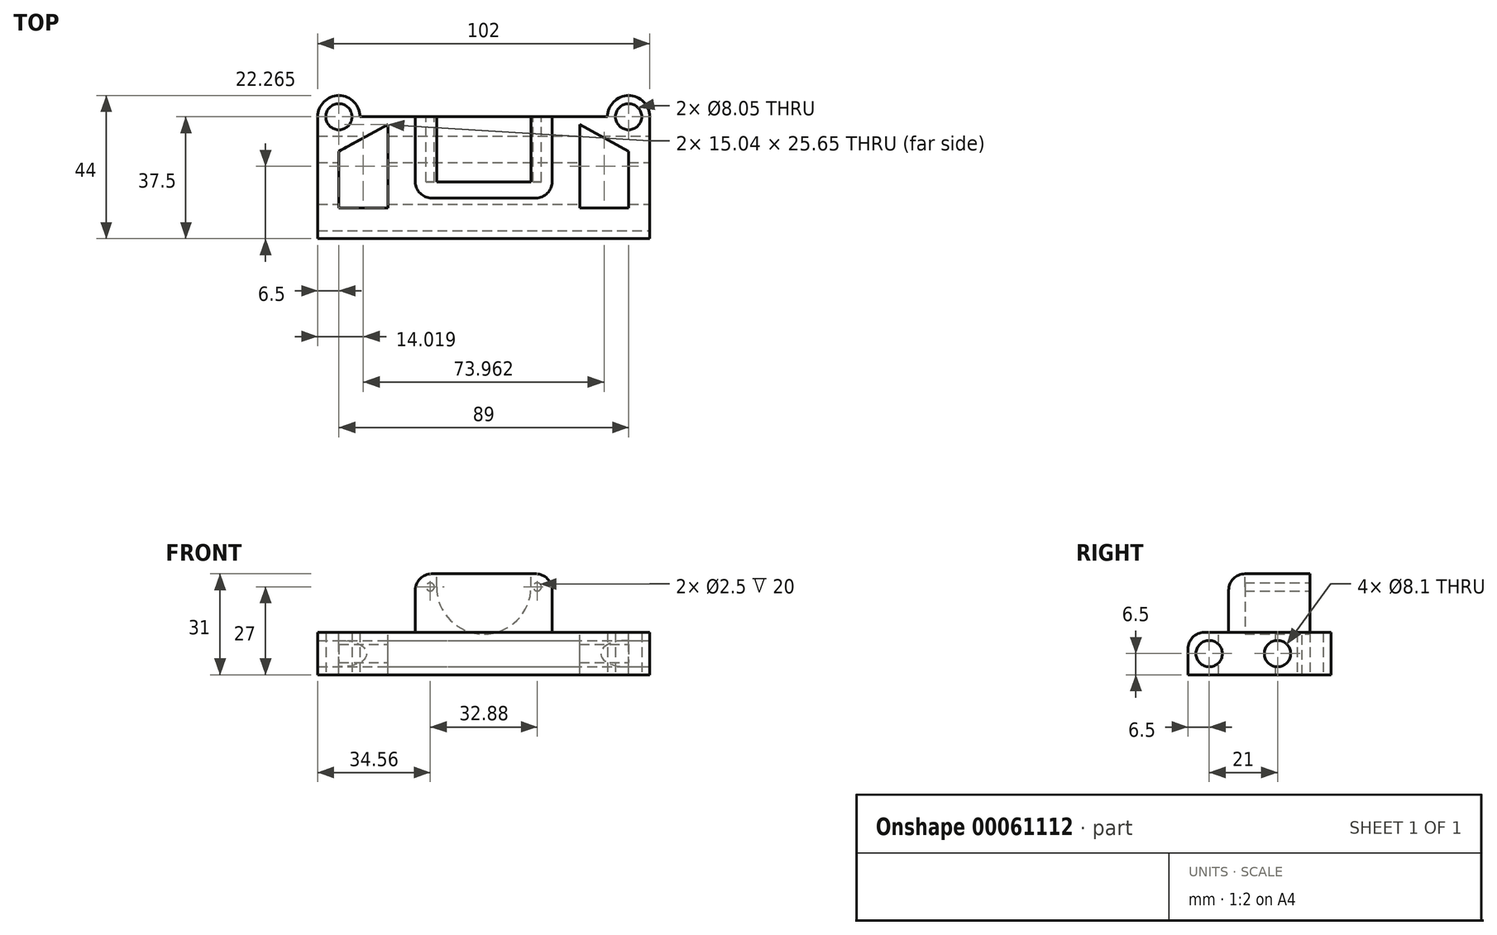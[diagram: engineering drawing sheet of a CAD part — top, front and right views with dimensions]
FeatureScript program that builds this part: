
annotation { "Feature Type Name" : "Feature", "Feature Type Description" : "" }
export const myFeature = defineFeature(function(context is Context, id is Id, definition is map)
    precondition{}
    {
        {
            var Q0;
            Q0=qCreatedBy(makeId("Top.planeOp"),FACE);
            var sketch = newSketch(context, id + "F0", { "sketchPlane" : qUnion([Q0])});
            skLineSegment(sketch, "E0", {"start": v(0, 0) * mm, "end": v(-38, 0) * mm});
            skLineSegment(sketch, "E1", {"start": v(0, 0) * mm, "end": v(38, 0) * mm});
            skCircle(sketch, "E2", {"center": v(-44.5, 0) * mm, "radius": 4.03 * mm});
            skCircle(sketch, "E3", {"center": v(44.5, 0) * mm, "radius": 4.03 * mm});
            skArc(sketch, "E4", {"start": v(-38, 0) * mm, "mid": v(-44.5, 6.5) * mm, "end": v(-51, 0) * mm});
            skArc(sketch, "E5", {"start": v(51, 0) * mm, "mid": v(44.5, 6.5) * mm, "end": v(38, 0) * mm});
            skLineSegment(sketch, "E6", {"start": v(0, 0) * mm, "end": v(0, -37.5) * mm, "construction": true});
            skLineSegment(sketch, "E7", {"start": v(0, -37.5) * mm, "end": v(-51, -37.5) * mm});
            skLineSegment(sketch, "E8", {"start": v(0, -37.5) * mm, "end": v(51, -37.5) * mm});
            skLineSegment(sketch, "E9", {"start": v(-51, -37.5) * mm, "end": v(-51, 0) * mm});
            skLineSegment(sketch, "E10", {"start": v(51, -37.5) * mm, "end": v(51, 0) * mm});
            skSolve(sketch);
        }
        {
            var Q0;
            Q0 = qSketchRegion(id + "F0", true);
            var Q1;
            Q1=makeQuery(id+"F0.imprint","IMPRINT",FACE,{"disambiguationData":[TD([[makeQuery(id+"F0.imprint","IMPRINT",EDGE,{"derivedFrom":sQuery(id+"F0.wireOp",EDGE,"E0")}),1.0]])]});
            extrude(context, id + "F1", {"entities" : qUnion([Q0, Q1]), "depth" : 13 * mm});
        }
        {
            var Q0;
            Q0=makeQuery(id+"F1.opExtrude","SWEPT_FACE",FACE,{"disambiguationData":[OSD([sQuery(id+"F0.wireOp",EDGE,"E10")])]});
            var sketch = newSketch(context, id + "F2", { "sketchPlane" : qUnion([Q0])});
            skCircle(sketch, "E11", {"center": v(-10, 6.5) * mm, "radius": 4.05 * mm});
            skCircle(sketch, "E12", {"center": v(-31, 6.5) * mm, "radius": 4.05 * mm});
            skLineSegment(sketch, "E13", {"start": v(0, 6.5) * mm, "end": v(-10, 6.5) * mm, "construction": true});
            skLineSegment(sketch, "E14", {"start": v(-10, 6.5) * mm, "end": v(-31, 6.5) * mm, "construction": true});
            skSolve(sketch);
        }
        {
            var Q0;
            Q0=makeQuery(id+"F2.imprint","IMPRINT",FACE,{"disambiguationData":[TD([[makeQuery(id+"F2.imprint","IMPRINT",EDGE,{"derivedFrom":sQuery(id+"F2.wireOp",EDGE,"E12")}),1.0]])]});
            var Q1;
            Q1=makeQuery(id+"F2.imprint","IMPRINT",FACE,{"disambiguationData":[TD([[makeQuery(id+"F2.imprint","IMPRINT",EDGE,{"derivedFrom":sQuery(id+"F2.wireOp",EDGE,"E11")}),1.0]])]});
            extrude(context, id + "F3", {"entities" : qUnion([Q0, Q1]), "operationType" : NewBodyOperationType.REMOVE, "oppositeDirection" : true, "depth" : 120 * mm});
        }
        {
            var Q0;
            Q0=makeQuery(id+"F1.opExtrude","CAP_FACE",FACE,{"disambiguationData":[OSD([sQuery(id+"F0.wireOp",EDGE,"E0"),sQuery(id+"F0.wireOp",EDGE,"E1"),sQuery(id+"F0.wireOp",EDGE,"E2"),sQuery(id+"F0.wireOp",EDGE,"E3"),sQuery(id+"F0.wireOp",EDGE,"E4"),sQuery(id+"F0.wireOp",EDGE,"E5"),sQuery(id+"F0.wireOp",EDGE,"E7"),sQuery(id+"F0.wireOp",EDGE,"E8"),sQuery(id+"F0.wireOp",EDGE,"E9"),sQuery(id+"F0.wireOp",EDGE,"E10")])],"isStart":false});
            var sketch = newSketch(context, id + "F4", { "sketchPlane" : qUnion([Q0])});
            skLineSegment(sketch, "E15", {"start": v(0, 0) * mm, "end": v(0, -25) * mm, "construction": true});
            skLineSegment(sketch, "E16", {"start": v(0, -25) * mm, "end": v(-21, -25) * mm});
            skLineSegment(sketch, "E17", {"start": v(-21, -25) * mm, "end": v(-21, 0) * mm});
            skLineSegment(sketch, "E18", {"start": v(0, -25) * mm, "end": v(21, -25) * mm});
            skLineSegment(sketch, "E19", {"start": v(21, -25) * mm, "end": v(21, 0) * mm});
            skLineSegment(sketch, "E20", {"start": v(21, 0) * mm, "end": v(-21, 0) * mm});
            skSolve(sketch);
        }
        {
            var Q0;
            Q0=makeQuery(id+"F4.imprint","IMPRINT",FACE,{"disambiguationData":[TD([[makeQuery(id+"F4.imprint","IMPRINT",EDGE,{"derivedFrom":sQuery(id+"F4.wireOp",EDGE,"E16")}),-1.0]])]});
            extrude(context, id + "F5", {"entities" : qUnion([Q0]), "operationType" : NewBodyOperationType.ADD, "depth" : 18 * mm});
        }
        {
            var Q0;
            Q0=makeQuery(id+"F5.boolean.opBoolean","MERGE",FACE,{"derivedFrom":[makeQuery(id+"F1.opExtrude","SWEPT_FACE",FACE,{"disambiguationData":[OSD([sQuery(id+"F0.wireOp",EDGE,"E0"),sQuery(id+"F0.wireOp",EDGE,"E1")])]}),makeQuery(id+"F5.opExtrude","SWEPT_FACE",FACE,{"disambiguationData":[OSD([sQuery(id+"F4.wireOp",EDGE,"E20")])]})]});
            var sketch = newSketch(context, id + "F6", { "sketchPlane" : qUnion([Q0])});
            skLineSegment(sketch, "E21", {"start": v(0, 31) * mm, "end": v(0, 27) * mm, "construction": true});
            skPoint(sketch, "E21.endSnap0", {"position": v(0, 31) * mm});
            skArc(sketch, "E22", {"start": v(-14.5, 27) * mm, "mid": v(0, 12.5) * mm, "end": v(14.5, 27) * mm});
            skLineSegment(sketch, "E23", {"start": v(0, 27) * mm, "end": v(-16.44, 27) * mm, "construction": true});
            skLineSegment(sketch, "E24", {"start": v(0, 27) * mm, "end": v(16.44, 27) * mm, "construction": true});
            skCircle(sketch, "E25", {"center": v(-16.44, 27) * mm, "radius": 1.25 * mm});
            skCircle(sketch, "E26", {"center": v(16.44, 27) * mm, "radius": 1.25 * mm});
            skLineSegment(sketch, "E27", {"start": v(-14.5, 27) * mm, "end": v(-14.5, 31) * mm});
            skLineSegment(sketch, "E28", {"start": v(14.5, 27) * mm, "end": v(14.5, 31) * mm});
            skSolve(sketch);
        }
        {
            var Q0;
            Q0=makeQuery(id+"F6.imprint","IMPRINT",FACE,{"disambiguationData":[TD([[makeQuery(id+"F6.imprint","IMPRINT",EDGE,{"derivedFrom":sQuery(id+"F6.wireOp",EDGE,"E22")}),1.0]])]});
            var Q1;
            Q1=makeQuery(id+"F6.imprint","IMPRINT",FACE,{"disambiguationData":[TD([[makeQuery(id+"F6.imprint","IMPRINT",EDGE,{"derivedFrom":sQuery(id+"F6.wireOp",EDGE,"E25")}),1.0]])]});
            var Q2;
            Q2=makeQuery(id+"F6.imprint","IMPRINT",FACE,{"disambiguationData":[TD([[makeQuery(id+"F6.imprint","IMPRINT",EDGE,{"derivedFrom":sQuery(id+"F6.wireOp",EDGE,"E26")}),1.0]])]});
            extrude(context, id + "F7", {"entities" : qUnion([Q0, Q1, Q2]), "operationType" : NewBodyOperationType.REMOVE, "oppositeDirection" : true, "depth" : 20 * mm});
        }
        {
            var Q0;
            Q0=makeQuery(id+"F5.opExtrude","CAP_EDGE",EDGE,{"disambiguationData":[OSD([sQuery(id+"F4.wireOp",EDGE,"E19")])],"isStart":false});
            var Q1;
            Q1=makeQuery(id+"F5.opExtrude","CAP_EDGE",EDGE,{"disambiguationData":[OSD([sQuery(id+"F4.wireOp",EDGE,"E17")])],"isStart":false});
            var Q2;
            Q2=makeQuery(id+"F5.opExtrude","CAP_EDGE",EDGE,{"disambiguationData":[OSD([sQuery(id+"F4.wireOp",EDGE,"E19")])],"isStart":true});
            var Q3;
            Q3=makeQuery(id+"F5.opExtrude","CAP_EDGE",EDGE,{"disambiguationData":[OSD([sQuery(id+"F4.wireOp",EDGE,"E17")])],"isStart":true});
            var Q4;
            Q4=makeQuery(id+"F5.opExtrude","CAP_EDGE",EDGE,{"disambiguationData":[OSD([sQuery(id+"F4.wireOp",EDGE,"E16"),sQuery(id+"F4.wireOp",EDGE,"E18")])],"isStart":false});
            var Q5;
            Q5=makeQuery(id+"F5.opExtrude","SWEPT_EDGE",EDGE,{"disambiguationData":[OSD([sQuery(id+"F4.wireOp",EDGE,"E18"),sQuery(id+"F4.wireOp",EDGE,"E19")])]});
            var Q6;
            Q6=makeQuery(id+"F5.opExtrude","SWEPT_EDGE",EDGE,{"disambiguationData":[OSD([sQuery(id+"F4.wireOp",EDGE,"E16"),sQuery(id+"F4.wireOp",EDGE,"E17")])]});
            var Q7;
            Q7=makeQuery(id+"F1.opExtrude","CAP_EDGE",EDGE,{"disambiguationData":[OSD([sQuery(id+"F0.wireOp",EDGE,"E7"),sQuery(id+"F0.wireOp",EDGE,"E8")])],"isStart":false});
            fillet(context, id + "F8", {"entities" : qUnion([Q0, Q1, Q2, Q3, Q4, Q5, Q6, Q7]), "radius" : 5 * mm, "tangentPropagation" : true, "allowEdgeOverflow" : false});
        }
        {
            var Q0;
            Q0=makeQuery(id+"F1.opExtrude","CAP_FACE",FACE,{"disambiguationData":[OSD([sQuery(id+"F0.wireOp",EDGE,"E0"),sQuery(id+"F0.wireOp",EDGE,"E1"),sQuery(id+"F0.wireOp",EDGE,"E2"),sQuery(id+"F0.wireOp",EDGE,"E3"),sQuery(id+"F0.wireOp",EDGE,"E4"),sQuery(id+"F0.wireOp",EDGE,"E5"),sQuery(id+"F0.wireOp",EDGE,"E7"),sQuery(id+"F0.wireOp",EDGE,"E8"),sQuery(id+"F0.wireOp",EDGE,"E9"),sQuery(id+"F0.wireOp",EDGE,"E10")])],"isStart":false});
            var sketch = newSketch(context, id + "F9", { "sketchPlane" : qUnion([Q0])});
            skLineSegment(sketch, "E29", {"start": v(-44.5, -10.61) * mm, "end": v(-44.5, -28.06) * mm});
            skLineSegment(sketch, "E30", {"start": v(-44.5, -28.06) * mm, "end": v(-29.46, -28.06) * mm});
            skLineSegment(sketch, "E31", {"start": v(-29.46, -28.06) * mm, "end": v(-29.46, -2.41) * mm});
            skLineSegment(sketch, "E32", {"start": v(-29.46, -2.41) * mm, "end": v(-44.5, -10.61) * mm});
            skLineSegment(sketch, "E33", {"start": v(44.5, -10.61) * mm, "end": v(44.5, -28.06) * mm});
            skLineSegment(sketch, "E34", {"start": v(44.5, -28.06) * mm, "end": v(29.46, -28.06) * mm});
            skLineSegment(sketch, "E35", {"start": v(29.46, -28.06) * mm, "end": v(29.46, -2.41) * mm});
            skLineSegment(sketch, "E36", {"start": v(29.46, -2.41) * mm, "end": v(44.5, -10.61) * mm});
            skPoint(sketch, "E37.orphan", {"position": v(-44.5, 0) * mm});
            skPoint(sketch, "E38.orphan", {"position": v(44.5, 0) * mm});
            skSolve(sketch);
        }
        {
            var Q0;
            Q0=makeQuery(id+"F9.imprint","IMPRINT",FACE,{"disambiguationData":[TD([[makeQuery(id+"F9.imprint","IMPRINT",EDGE,{"derivedFrom":sQuery(id+"F9.wireOp",EDGE,"E33")}),-1.0]])]});
            var Q1;
            Q1=makeQuery(id+"F9.imprint","IMPRINT",FACE,{"disambiguationData":[TD([[makeQuery(id+"F9.imprint","IMPRINT",EDGE,{"derivedFrom":sQuery(id+"F9.wireOp",EDGE,"E29")}),1.0]])]});
            extrude(context, id + "F10", {"entities" : qUnion([Q0, Q1]), "operationType" : NewBodyOperationType.REMOVE, "oppositeDirection" : true, "depth" : 25 * mm});
        }
    });
